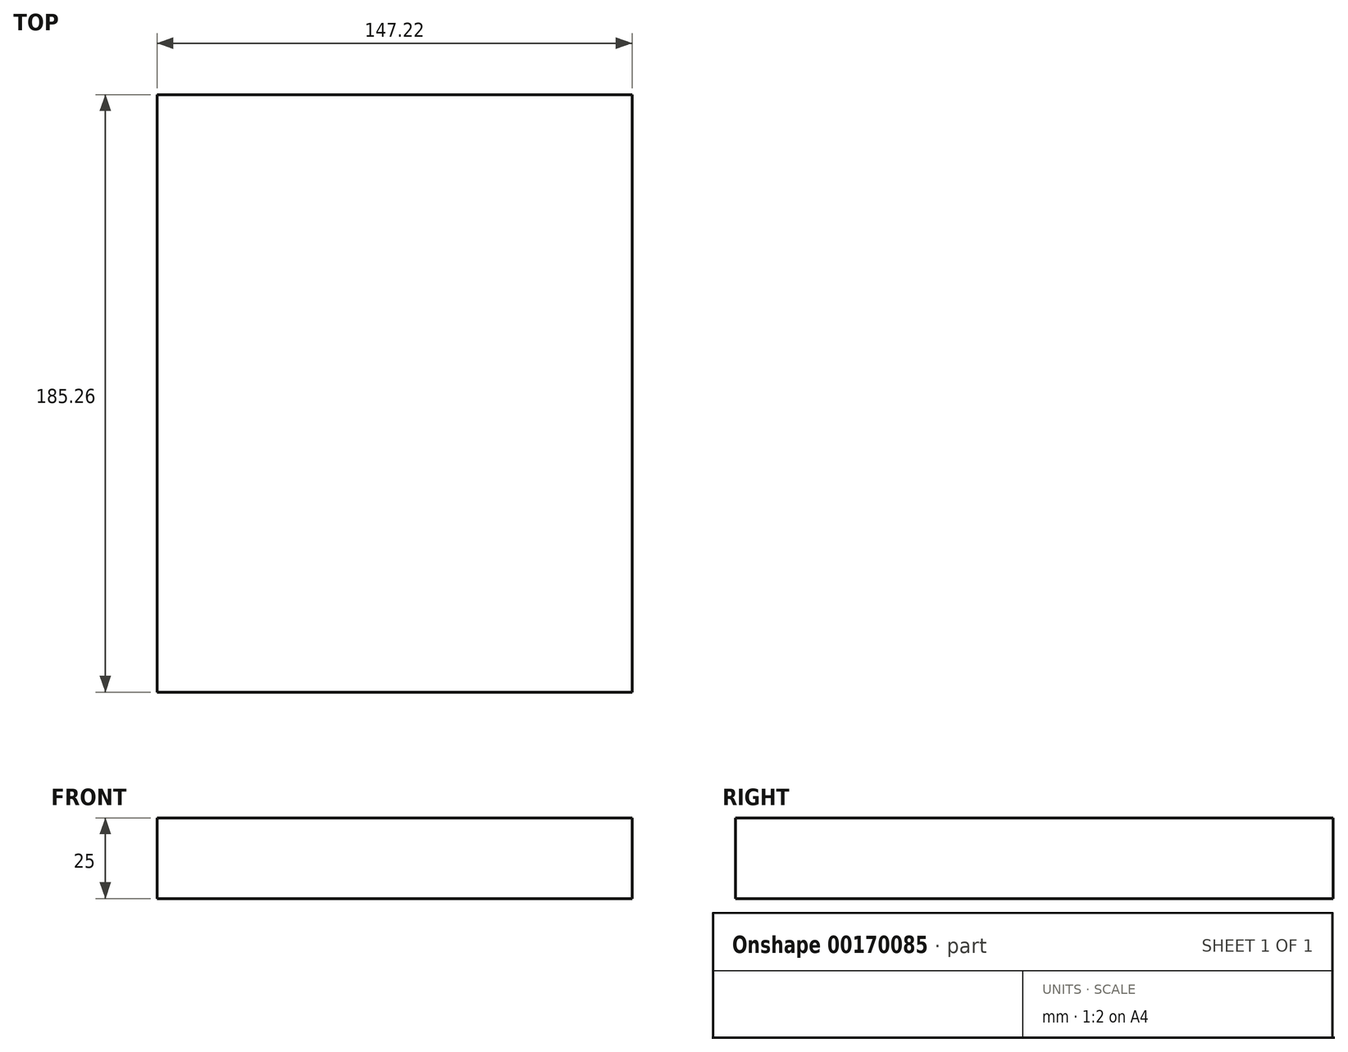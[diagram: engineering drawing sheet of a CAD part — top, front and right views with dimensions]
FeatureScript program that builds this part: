
annotation { "Feature Type Name" : "Feature", "Feature Type Description" : "" }
export const myFeature = defineFeature(function(context is Context, id is Id, definition is map)
    precondition{}
    {
        {
            var Q0;
            Q0=qCreatedBy(makeId("Top.planeOp"),FACE);
            var sketch = newSketch(context, id + "F0", { "sketchPlane" : qUnion([Q0])});
            skLineSegment(sketch, "E0.bottom", {"start": v(-73.61, -92.63) * mm, "end": v(73.61, -92.63) * mm});
            skLineSegment(sketch, "E0.top", {"start": v(-73.61, 92.63) * mm, "end": v(73.61, 92.63) * mm});
            skLineSegment(sketch, "E0.left", {"start": v(-73.61, -92.63) * mm, "end": v(-73.61, 92.63) * mm});
            skLineSegment(sketch, "E0.right", {"start": v(73.61, -92.63) * mm, "end": v(73.61, 92.63) * mm});
            skPoint(sketch, "E0.middle", {"position": v(0, 0) * mm});
            skSolve(sketch);
        }
        {
            var Q0;
            Q0 = qSketchRegion(id + "F0", true);
            extrude(context, id + "F1", {"entities" : qUnion([Q0]), "depth" : 25 * mm});
        }
    });
